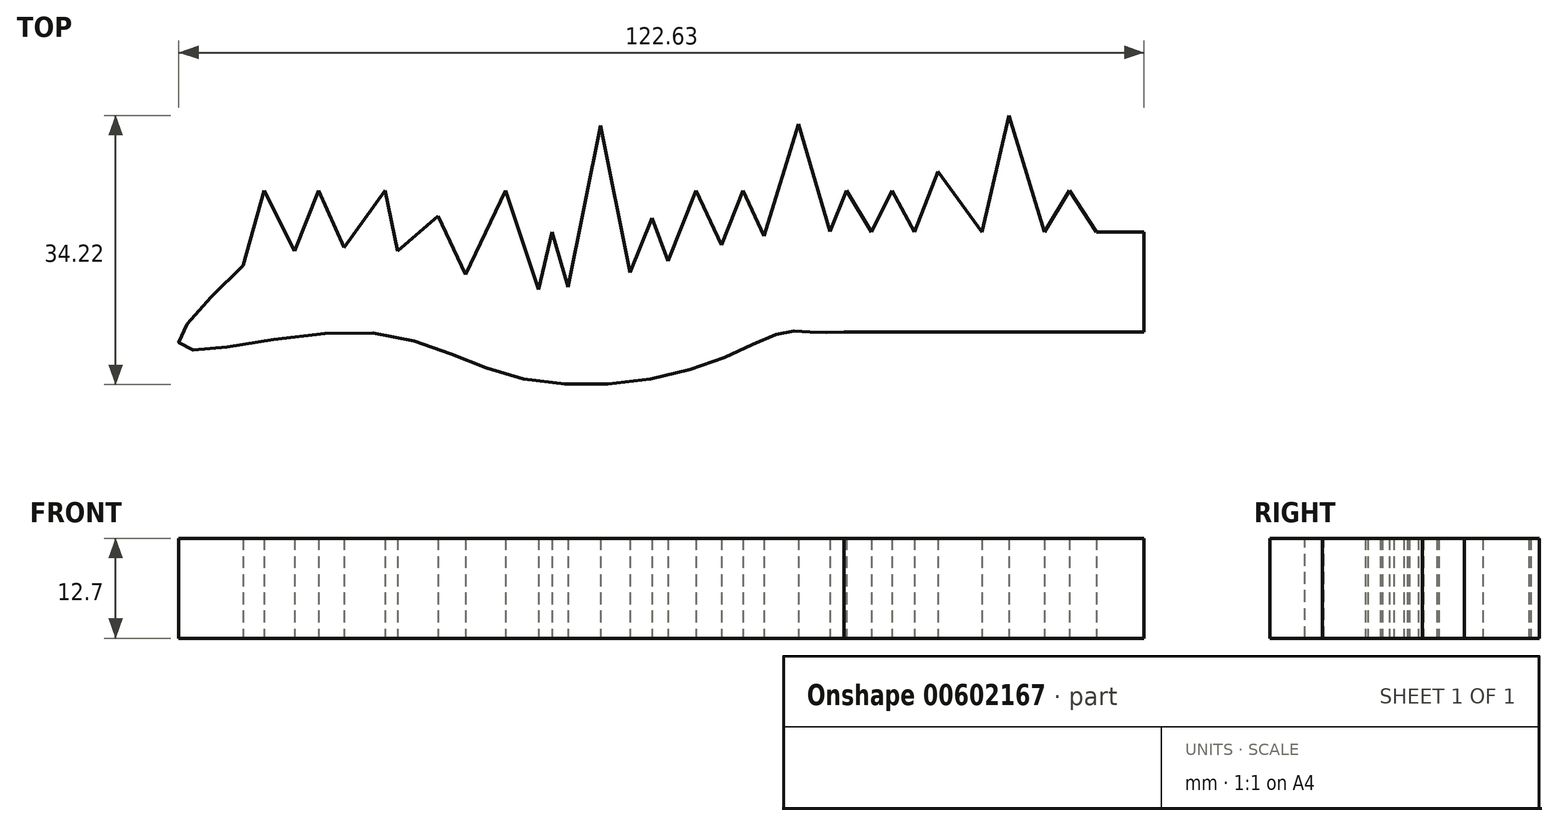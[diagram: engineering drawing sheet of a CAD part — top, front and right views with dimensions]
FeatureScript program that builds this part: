
annotation { "Feature Type Name" : "Feature", "Feature Type Description" : "" }
export const myFeature = defineFeature(function(context is Context, id is Id, definition is map)
    precondition{}
    {
        {
            var Q0;
            Q0=qCreatedBy(makeId("Top.planeOp"),FACE);
            var sketch = newSketch(context, id + "F0", { "sketchPlane" : qUnion([Q0])});
            skLineSegment(sketch, "E0", {"start": v(29.16, 14.48) * mm, "end": v(29.16, 1.78) * mm});
            skLineSegment(sketch, "E1", {"start": v(29.16, 1.78) * mm, "end": v(-8.94, 1.78) * mm});
            skLineSegment(sketch, "E2", {"start": v(29.16, 14.48) * mm, "end": v(-8.94, 14.48) * mm});
            skFitSpline(sketch, "E3", {"points": [v(-8.94, 14.48) * mm, v(-14.78, 14.48) * mm, v(-27.23, 12.1) * mm, v(-50.3, 7.32) * mm, v(-69.91, 12.62) * mm, v(-85.29, 9.97) * mm, v(-85.29, 10.24) * mm], "startDerivative": vector(-44.62, 1.78) * mm, "endDerivative": vector(4.9, 12.5) * mm});
            skFitSpline(sketch, "E4", {"points": [v(-8.94, 1.78) * mm, v(-12.92, 1.78) * mm, v(-16.63, 1.78) * mm, v(-26.97, -2.49) * mm, v(-50.03, -4.08) * mm, v(-70.7, 1.78) * mm, v(-93.24, 0) * mm, v(-85.29, 10.24) * mm], "startDerivative": vector(-51.39, -1.78) * mm, "endDerivative": vector(96.78, 93.2) * mm});
            skLineSegment(sketch, "E5", {"start": v(29.16, 14.48) * mm, "end": v(26.65, 19.78) * mm});
            skLineSegment(sketch, "E6", {"start": v(26.31, 19.78) * mm, "end": v(23.13, 14.48) * mm});
            skLineSegment(sketch, "E7", {"start": v(23.13, 14.48) * mm, "end": v(19.69, 19.78) * mm});
            skLineSegment(sketch, "E8", {"start": v(19.69, 19.78) * mm, "end": v(16.5, 14.48) * mm});
            skLineSegment(sketch, "E9", {"start": v(16.5, 14.48) * mm, "end": v(12, 29.33) * mm});
            skLineSegment(sketch, "E10", {"start": v(12, 29.33) * mm, "end": v(8.55, 14.48) * mm});
            skLineSegment(sketch, "E11", {"start": v(8.55, 14.48) * mm, "end": v(2.99, 22.17) * mm});
            skLineSegment(sketch, "E12", {"start": v(2.99, 22.17) * mm, "end": v(0, 14.48) * mm});
            skLineSegment(sketch, "E13", {"start": v(0, 14.48) * mm, "end": v(-2.85, 19.78) * mm});
            skLineSegment(sketch, "E14", {"start": v(-2.85, 19.78) * mm, "end": v(-5.5, 14.48) * mm});
            skLineSegment(sketch, "E15", {"start": v(-5.5, 14.48) * mm, "end": v(-8.68, 19.78) * mm});
            skLineSegment(sketch, "E16", {"start": v(-8.68, 19.78) * mm, "end": v(-10.76, 14.55) * mm});
            skLineSegment(sketch, "E17", {"start": v(-10.76, 14.55) * mm, "end": v(-14.78, 28.23) * mm});
            skLineSegment(sketch, "E18", {"start": v(-14.78, 28.23) * mm, "end": v(-19.15, 13.97) * mm});
            skLineSegment(sketch, "E19", {"start": v(-19.15, 13.97) * mm, "end": v(-21.78, 19.78) * mm});
            skLineSegment(sketch, "E20", {"start": v(-21.78, 19.78) * mm, "end": v(-24.54, 12.83) * mm});
            skLineSegment(sketch, "E21", {"start": v(-24.54, 12.83) * mm, "end": v(-27.77, 19.78) * mm});
            skLineSegment(sketch, "E22", {"start": v(-27.77, 19.78) * mm, "end": v(-31.32, 10.84) * mm});
            skLineSegment(sketch, "E23", {"start": v(-31.32, 10.84) * mm, "end": v(-33.36, 16.31) * mm});
            skLineSegment(sketch, "E24", {"start": v(-33.36, 16.31) * mm, "end": v(-36.12, 9.36) * mm});
            skLineSegment(sketch, "E25", {"start": v(-36.12, 9.36) * mm, "end": v(-39.92, 28) * mm});
            skLineSegment(sketch, "E26", {"start": v(-39.92, 28) * mm, "end": v(-44, 7.54) * mm});
            skLineSegment(sketch, "E27", {"start": v(-44, 7.54) * mm, "end": v(-46.06, 14.48) * mm});
            skLineSegment(sketch, "E28", {"start": v(-46.06, 14.48) * mm, "end": v(-47.74, 7.22) * mm});
            skLineSegment(sketch, "E29", {"start": v(-47.74, 7.22) * mm, "end": v(-51.97, 19.78) * mm});
            skLineSegment(sketch, "E30", {"start": v(-51.97, 19.78) * mm, "end": v(-57, 9.1) * mm});
            skLineSegment(sketch, "E31", {"start": v(-57, 9.1) * mm, "end": v(-60.55, 16.53) * mm});
            skLineSegment(sketch, "E32", {"start": v(-60.55, 16.53) * mm, "end": v(-65.7, 12.1) * mm});
            skLineSegment(sketch, "E33", {"start": v(-65.7, 12.1) * mm, "end": v(-67.24, 19.78) * mm});
            skLineSegment(sketch, "E34", {"start": v(-67.24, 19.78) * mm, "end": v(-72.44, 12.53) * mm});
            skLineSegment(sketch, "E35", {"start": v(-72.44, 12.53) * mm, "end": v(-75.71, 19.78) * mm});
            skLineSegment(sketch, "E36", {"start": v(-75.71, 19.78) * mm, "end": v(-78.77, 12.1) * mm});
            skLineSegment(sketch, "E37", {"start": v(-78.77, 12.1) * mm, "end": v(-82.62, 19.78) * mm});
            skLineSegment(sketch, "E38", {"start": v(-82.62, 19.78) * mm, "end": v(-85.29, 10.24) * mm});
            skSolve(sketch);
        }
        {
            var Q0;
            {var subQ17=sQuery(id+"F0.wireOp",EDGE,"E0");Q0=makeQuery(id+"F0.imprint","IMPRINT",FACE,{"disambiguationData":[TD([[makeQuery(id+"F0.imprint","IMPRINT",EDGE,{"derivedFrom":subQ17}),-1.0]])]});}
            var Q1;
            {var subQ2=sQuery(id+"F0.wireOp",EDGE,"E35");Q1=makeQuery(id+"F0.imprint","IMPRINT",FACE,{"disambiguationData":[TD([[makeQuery(id+"F0.imprint","IMPRINT",EDGE,{"derivedFrom":subQ2}),1.0]])]});}
            var Q2;
            {var subQ0=sQuery(id+"F0.wireOp",EDGE,"E33");Q2=makeQuery(id+"F0.imprint","IMPRINT",FACE,{"disambiguationData":[TD([[makeQuery(id+"F0.imprint","IMPRINT",EDGE,{"derivedFrom":subQ0}),1.0]])]});}
            var Q3;
            {var subQ0=sQuery(id+"F0.wireOp",EDGE,"E29");Q3=makeQuery(id+"F0.imprint","IMPRINT",FACE,{"disambiguationData":[TD([[makeQuery(id+"F0.imprint","IMPRINT",EDGE,{"derivedFrom":subQ0}),1.0]])]});}
            var Q4;
            {var subQ0=sQuery(id+"F0.wireOp",EDGE,"E27");Q4=makeQuery(id+"F0.imprint","IMPRINT",FACE,{"disambiguationData":[TD([[makeQuery(id+"F0.imprint","IMPRINT",EDGE,{"derivedFrom":subQ0}),1.0]])]});}
            var Q5;
            {var subQ0=sQuery(id+"F0.wireOp",EDGE,"E25");Q5=makeQuery(id+"F0.imprint","IMPRINT",FACE,{"disambiguationData":[TD([[makeQuery(id+"F0.imprint","IMPRINT",EDGE,{"derivedFrom":subQ0}),1.0]])]});}
            var Q6;
            {var subQ0=sQuery(id+"F0.wireOp",EDGE,"E23");Q6=makeQuery(id+"F0.imprint","IMPRINT",FACE,{"disambiguationData":[TD([[makeQuery(id+"F0.imprint","IMPRINT",EDGE,{"derivedFrom":subQ0}),1.0]])]});}
            var Q7;
            {var subQ0=sQuery(id+"F0.wireOp",EDGE,"E21");Q7=makeQuery(id+"F0.imprint","IMPRINT",FACE,{"disambiguationData":[TD([[makeQuery(id+"F0.imprint","IMPRINT",EDGE,{"derivedFrom":subQ0}),1.0]])]});}
            var Q8;
            {var subQ0=sQuery(id+"F0.wireOp",EDGE,"E19");Q8=makeQuery(id+"F0.imprint","IMPRINT",FACE,{"disambiguationData":[TD([[makeQuery(id+"F0.imprint","IMPRINT",EDGE,{"derivedFrom":subQ0}),1.0]])]});}
            var Q9;
            {var subQ0=sQuery(id+"F0.wireOp",EDGE,"E13");Q9=makeQuery(id+"F0.imprint","IMPRINT",FACE,{"disambiguationData":[TD([[makeQuery(id+"F0.imprint","IMPRINT",EDGE,{"derivedFrom":subQ0}),1.0]])]});}
            var Q10;
            {var subQ0=sQuery(id+"F0.wireOp",EDGE,"E11");Q10=makeQuery(id+"F0.imprint","IMPRINT",FACE,{"disambiguationData":[TD([[makeQuery(id+"F0.imprint","IMPRINT",EDGE,{"derivedFrom":subQ0}),1.0]])]});}
            var Q11;
            {var subQ0=sQuery(id+"F0.wireOp",EDGE,"E9");Q11=makeQuery(id+"F0.imprint","IMPRINT",FACE,{"disambiguationData":[TD([[makeQuery(id+"F0.imprint","IMPRINT",EDGE,{"derivedFrom":subQ0}),1.0]])]});}
            var Q12;
            {var subQ0=sQuery(id+"F0.wireOp",EDGE,"E7");Q12=makeQuery(id+"F0.imprint","IMPRINT",FACE,{"disambiguationData":[TD([[makeQuery(id+"F0.imprint","IMPRINT",EDGE,{"derivedFrom":subQ0}),1.0]])]});}
            var Q13;
            {var subQ0=sQuery(id+"F0.wireOp",EDGE,"nSKzZAHa-ke61-IUcW-8V3E-Eo5Ka8OZE2yF");Q13=makeQuery(id+"F0.imprint","IMPRINT",FACE,{"disambiguationData":[TD([[makeQuery(id+"F0.imprint","IMPRINT",EDGE,{"derivedFrom":subQ0}),1.0]])]});}
            var Q14;
            {var subQ0=sQuery(id+"F0.wireOp",EDGE,"RJ8wtO1g-SZe7-Dw1V-VfI8-30BLLILN83pW");Q14=makeQuery(id+"F0.imprint","IMPRINT",FACE,{"disambiguationData":[TD([[makeQuery(id+"F0.imprint","IMPRINT",EDGE,{"derivedFrom":subQ0}),1.0]])]});}
            var Q15;
            {var subQ0=sQuery(id+"F0.wireOp",EDGE,"X3L38sVU-dUHn-eH1F-XJho-OxI67xcJqkFG");Q15=makeQuery(id+"F0.imprint","IMPRINT",FACE,{"disambiguationData":[TD([[makeQuery(id+"F0.imprint","IMPRINT",EDGE,{"derivedFrom":subQ0}),1.0]])]});}
            var Q16;
            {var subQ0=sQuery(id+"F0.wireOp",EDGE,"XF6P9p72-9Ona-jqsL-RlSC-t15IDcJOiF58");Q16=makeQuery(id+"F0.imprint","IMPRINT",FACE,{"disambiguationData":[TD([[makeQuery(id+"F0.imprint","IMPRINT",EDGE,{"derivedFrom":subQ0}),1.0]])]});}
            var Q17;
            {var subQ0=sQuery(id+"F0.wireOp",EDGE,"dwEvmPCV-S963-GgOa-DC8x-lDDMrownqrc6");Q17=makeQuery(id+"F0.imprint","IMPRINT",FACE,{"disambiguationData":[TD([[makeQuery(id+"F0.imprint","IMPRINT",EDGE,{"derivedFrom":subQ0}),1.0]])]});}
            var Q18;
            {var subQ0=sQuery(id+"F0.wireOp",EDGE,"E5");Q18=makeQuery(id+"F0.imprint","IMPRINT",FACE,{"disambiguationData":[TD([[makeQuery(id+"F0.imprint","IMPRINT",EDGE,{"derivedFrom":subQ0}),1.0]])]});}
            var Q19;
            {var subQ3=sQuery(id+"F0.wireOp",EDGE,"E15");Q19=makeQuery(id+"F0.imprint","IMPRINT",FACE,{"disambiguationData":[TD([[makeQuery(id+"F0.imprint","IMPRINT",EDGE,{"derivedFrom":subQ3}),1.0]])]});}
            var Q20;
            {var subQ0=sQuery(id+"F0.wireOp",EDGE,"E31");Q20=makeQuery(id+"F0.imprint","IMPRINT",FACE,{"disambiguationData":[TD([[makeQuery(id+"F0.imprint","IMPRINT",EDGE,{"derivedFrom":subQ0}),1.0]])]});}
            extrude(context, id + "F1", {"entities" : qUnion([Q0, Q1, Q2, Q3, Q4, Q5, Q6, Q7, Q8, Q9, Q10, Q11, Q12, Q13, Q14, Q15, Q16, Q17, Q18, Q19, Q20]), "depth" : 12.7 * mm, "offsetDistance" : 25.4 * mm});
        }
    });
